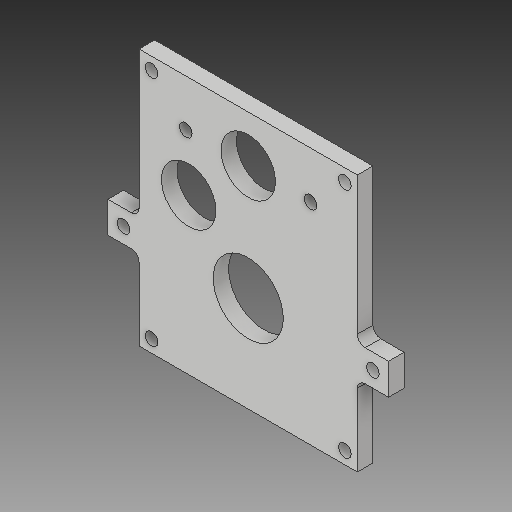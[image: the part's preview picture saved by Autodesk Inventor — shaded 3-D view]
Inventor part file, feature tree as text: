
AUTODESK INVENTOR PART (.ipt)
format: ipt  version: 2018 (Build 220112000, 112)  size: 178,176 bytes
history: native  units: in
note: dims shown in document units (in); Inventor stores cm internally (conversion verified against a paired STEP export)
features: extrude x3, sketch x3, fillet x1
ambient origin geometry x8: Origin, YZ Plane, XZ Plane, XY Plane, X Axis, Y Axis, Z Axis, Center Point
bodies: Solid1 (feature_tree)
feature tree (7):
  extrude  "Extrusion1"  Depth=1.35in
  extrude  "Extrusion2"  Depth=0.875in
  extrude  "Extrusion3"  Depth=0.125in
  fillet  "Fillet1"  Radius=1.0in
  sketch  "Sketch1"  dims[d0=1.125in d1=1.35in]
  sketch  "Sketch2"  dims[d2=135.0deg d3=0.875in]
  sketch  "Sketch3"  dims[d7=0.882in d8=0.875in d9=1.0in d10=2.0in d11=0.2031in d12=0.75in d13=4.125in d14=1.75in d15=0.25in d16=0.0in d17=1.75in d18=0.2in d19=0.2in d20=0.2031in d21=1.0in d22=0.0in d23=0.2031in d24=0.25in d25=0.5in d26=0.5in d27=0.2031in d28=0.25in d29=0.0in d30=0.125in]
